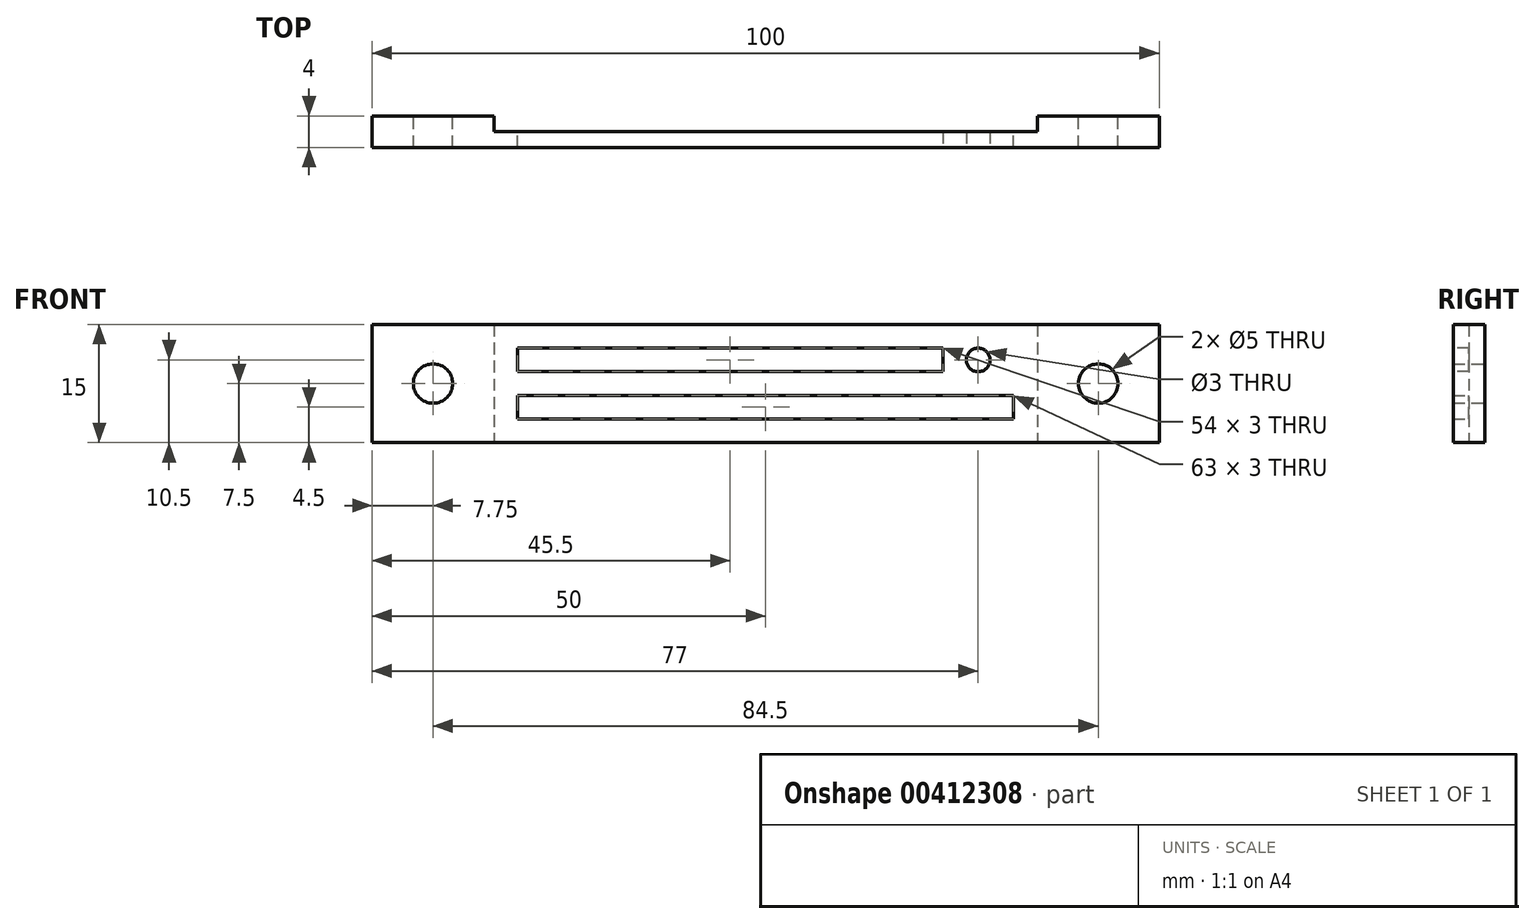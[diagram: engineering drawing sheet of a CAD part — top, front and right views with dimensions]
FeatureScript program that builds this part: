
annotation { "Feature Type Name" : "Feature", "Feature Type Description" : "" }
export const myFeature = defineFeature(function(context is Context, id is Id, definition is map)
    precondition{}
    {
        {
            var Q0;
            Q0=qCreatedBy(makeId("Front.planeOp"),FACE);
            var sketch = newSketch(context, id + "F0", { "sketchPlane" : qUnion([Q0])});
            skLineSegment(sketch, "E0.bottom", {"start": v(50, 7.5) * mm, "end": v(-50, 7.5) * mm});
            skLineSegment(sketch, "E0.top", {"start": v(50, -7.5) * mm, "end": v(-50, -7.5) * mm});
            skLineSegment(sketch, "E0.left", {"start": v(50, 7.5) * mm, "end": v(50, -7.5) * mm});
            skLineSegment(sketch, "E0.right", {"start": v(-50, 7.5) * mm, "end": v(-50, -7.5) * mm});
            skPoint(sketch, "E0.middle", {"position": v(0, 0) * mm});
            skLineSegment(sketch, "E1.bottom", {"start": v(31.5, 4.5) * mm, "end": v(-31.5, 4.5) * mm});
            skLineSegment(sketch, "E1.top", {"start": v(31.5, 1.5) * mm, "end": v(-31.5, 1.5) * mm});
            skLineSegment(sketch, "E1.left", {"start": v(31.5, 4.5) * mm, "end": v(31.5, 1.5) * mm});
            skLineSegment(sketch, "E1.right", {"start": v(-31.5, 4.5) * mm, "end": v(-31.5, 1.5) * mm});
            skPoint(sketch, "E1.middle", {"position": v(0, 3) * mm});
            skLineSegment(sketch, "E2.bottom", {"start": v(31.5, -1.5) * mm, "end": v(-31.5, -1.5) * mm});
            skLineSegment(sketch, "E2.top", {"start": v(31.5, -4.5) * mm, "end": v(-31.5, -4.5) * mm});
            skLineSegment(sketch, "E2.left", {"start": v(31.5, -1.5) * mm, "end": v(31.5, -4.5) * mm});
            skLineSegment(sketch, "E2.right", {"start": v(-31.5, -1.5) * mm, "end": v(-31.5, -4.5) * mm});
            skPoint(sketch, "E2.middle", {"position": v(0, -3) * mm});
            skSolve(sketch);
        }
        {
            var Q0;
            Q0 = qSketchRegion(id + "F0", true);
            extrude(context, id + "F1", {"entities" : qUnion([Q0]), "depth" : 4 * mm});
        }
        {
            var Q0;
            Q0=makeQuery(id+"F1.opExtrude","CAP_FACE",FACE,{"disambiguationData":[OSD([sQuery(id+"F0.wireOp",EDGE,"E0.bottom"),sQuery(id+"F0.wireOp",EDGE,"E0.top"),sQuery(id+"F0.wireOp",EDGE,"E0.left"),sQuery(id+"F0.wireOp",EDGE,"E0.right"),sQuery(id+"F0.wireOp",EDGE,"E1.bottom"),sQuery(id+"F0.wireOp",EDGE,"E1.top"),sQuery(id+"F0.wireOp",EDGE,"E1.left"),sQuery(id+"F0.wireOp",EDGE,"E1.right"),sQuery(id+"F0.wireOp",EDGE,"E2.bottom"),sQuery(id+"F0.wireOp",EDGE,"E2.top"),sQuery(id+"F0.wireOp",EDGE,"E2.left"),sQuery(id+"F0.wireOp",EDGE,"E2.right")])],"isStart":true});
            var sketch = newSketch(context, id + "F2", { "sketchPlane" : qUnion([Q0])});
            skLineSegment(sketch, "E3.bottom", {"start": v(34.5, 7.5) * mm, "end": v(-34.5, 7.5) * mm});
            skLineSegment(sketch, "E3.top", {"start": v(34.5, -7.5) * mm, "end": v(-34.5, -7.5) * mm});
            skLineSegment(sketch, "E3.left", {"start": v(34.5, 7.5) * mm, "end": v(34.5, -7.5) * mm});
            skLineSegment(sketch, "E3.right", {"start": v(-34.5, 7.5) * mm, "end": v(-34.5, -7.5) * mm});
            skPoint(sketch, "E3.middle", {"position": v(0, 0) * mm});
            skSolve(sketch);
        }
        {
            var Q0;
            Q0 = qSketchRegion(id + "F2", true);
            extrude(context, id + "F3", {"entities" : qUnion([Q0]), "operationType" : NewBodyOperationType.REMOVE, "oppositeDirection" : true, "depth" : 2 * mm});
        }
        {
            var Q0;
            {var subQ0=sQuery(id+"F0.wireOp",EDGE,"E0.bottom");var subQ1=sQuery(id+"F0.wireOp",EDGE,"E0.top");var subQ2=sQuery(id+"F0.wireOp",EDGE,"E0.left");Q0=makeQuery(id+"F3.boolean.opBoolean","SPLIT",FACE,{"disambiguationData":[TD([makeQuery(id+"F1.opExtrude","SWEPT_FACE",FACE,{"disambiguationData":[OSD([subQ2])]})])],"derivedFrom":makeQuery(id+"F1.opExtrude","CAP_FACE",FACE,{"disambiguationData":[OSD([subQ0,subQ1,subQ2,sQuery(id+"F0.wireOp",EDGE,"E0.right"),sQuery(id+"F0.wireOp",EDGE,"E1.bottom"),sQuery(id+"F0.wireOp",EDGE,"E1.top"),sQuery(id+"F0.wireOp",EDGE,"E1.left"),sQuery(id+"F0.wireOp",EDGE,"E1.right"),sQuery(id+"F0.wireOp",EDGE,"E2.bottom"),sQuery(id+"F0.wireOp",EDGE,"E2.top"),sQuery(id+"F0.wireOp",EDGE,"E2.left"),sQuery(id+"F0.wireOp",EDGE,"E2.right")])],"isStart":true})});}
            var sketch = newSketch(context, id + "F4", { "sketchPlane" : qUnion([Q0])});
            skLineSegment(sketch, "E4", {"start": v(-34.5, 7.5) * mm, "end": v(-50, -7.5) * mm, "construction": true});
            skLineSegment(sketch, "E5", {"start": v(-50, -7.5) * mm, "end": v(-50, 7.5) * mm, "construction": true});
            skLineSegment(sketch, "E6", {"start": v(-50, 7.5) * mm, "end": v(-34.5, -7.5) * mm, "construction": true});
            skCircle(sketch, "E7", {"center": v(-42.25, 0) * mm, "radius": 2.5 * mm});
            skSolve(sketch);
        }
        {
            var Q0;
            Q0 = qSketchRegion(id + "F4", true);
            extrude(context, id + "F5", {"entities" : qUnion([Q0]), "operationType" : NewBodyOperationType.REMOVE, "oppositeDirection" : true, "depth" : 25 * mm});
        }
        {
            var Q0;
            {var subQ0=sQuery(id+"F0.wireOp",EDGE,"E0.bottom");var subQ1=sQuery(id+"F0.wireOp",EDGE,"E0.right");var subQ2=sQuery(id+"F0.wireOp",EDGE,"E0.top");Q0=makeQuery(id+"F3.boolean.opBoolean","SPLIT",FACE,{"disambiguationData":[TD([makeQuery(id+"F1.opExtrude","SWEPT_FACE",FACE,{"disambiguationData":[OSD([subQ1])]})])],"derivedFrom":makeQuery(id+"F1.opExtrude","CAP_FACE",FACE,{"disambiguationData":[OSD([subQ0,subQ2,sQuery(id+"F0.wireOp",EDGE,"E0.left"),subQ1,sQuery(id+"F0.wireOp",EDGE,"E1.bottom"),sQuery(id+"F0.wireOp",EDGE,"E1.top"),sQuery(id+"F0.wireOp",EDGE,"E1.left"),sQuery(id+"F0.wireOp",EDGE,"E1.right"),sQuery(id+"F0.wireOp",EDGE,"E2.bottom"),sQuery(id+"F0.wireOp",EDGE,"E2.top"),sQuery(id+"F0.wireOp",EDGE,"E2.left"),sQuery(id+"F0.wireOp",EDGE,"E2.right")])],"isStart":true})});}
            var sketch = newSketch(context, id + "F6", { "sketchPlane" : qUnion([Q0])});
            skLineSegment(sketch, "E8", {"start": v(34.5, 7.5) * mm, "end": v(50, -7.5) * mm, "construction": true});
            skCircle(sketch, "E9", {"center": v(42.25, 0) * mm, "radius": 2.5 * mm});
            skSolve(sketch);
        }
        {
            var Q0;
            Q0 = qSketchRegion(id + "F6", true);
            extrude(context, id + "F7", {"entities" : qUnion([Q0]), "operationType" : NewBodyOperationType.REMOVE, "oppositeDirection" : true, "depth" : 25 * mm});
        }
        {
            var Q0;
            Q0=makeQuery(id+"F1.opExtrude","CAP_FACE",FACE,{"disambiguationData":[OSD([sQuery(id+"F0.wireOp",EDGE,"E0.bottom"),sQuery(id+"F0.wireOp",EDGE,"E0.top"),sQuery(id+"F0.wireOp",EDGE,"E0.left"),sQuery(id+"F0.wireOp",EDGE,"E0.right"),sQuery(id+"F0.wireOp",EDGE,"E1.bottom"),sQuery(id+"F0.wireOp",EDGE,"E1.top"),sQuery(id+"F0.wireOp",EDGE,"E1.left"),sQuery(id+"F0.wireOp",EDGE,"E1.right"),sQuery(id+"F0.wireOp",EDGE,"E2.bottom"),sQuery(id+"F0.wireOp",EDGE,"E2.top"),sQuery(id+"F0.wireOp",EDGE,"E2.left"),sQuery(id+"F0.wireOp",EDGE,"E2.right")])],"isStart":false});
            var sketch = newSketch(context, id + "F8", { "sketchPlane" : qUnion([Q0])});
            skLineSegment(sketch, "E10.bottom", {"start": v(31.5, 4.5) * mm, "end": v(22.5, 4.5) * mm});
            skLineSegment(sketch, "E10.top", {"start": v(31.5, 1.5) * mm, "end": v(22.5, 1.5) * mm});
            skLineSegment(sketch, "E10.left", {"start": v(31.5, 4.5) * mm, "end": v(31.5, 1.5) * mm});
            skLineSegment(sketch, "E10.right", {"start": v(22.5, 4.5) * mm, "end": v(22.5, 1.5) * mm});
            skSolve(sketch);
        }
        {
            var Q0;
            Q0 = qSketchRegion(id + "F8", true);
            extrude(context, id + "F9", {"entities" : qUnion([Q0]), "operationType" : NewBodyOperationType.ADD, "oppositeDirection" : true, "depth" : 2 * mm});
        }
        {
            var Q0;
            Q0=makeQuery(id+"F9.boolean.opBoolean","MERGE",FACE,{"derivedFrom":[makeQuery(id+"F1.opExtrude","CAP_FACE",FACE,{"disambiguationData":[OSD([sQuery(id+"F0.wireOp",EDGE,"E0.bottom"),sQuery(id+"F0.wireOp",EDGE,"E0.top"),sQuery(id+"F0.wireOp",EDGE,"E0.left"),sQuery(id+"F0.wireOp",EDGE,"E0.right"),sQuery(id+"F0.wireOp",EDGE,"E1.bottom"),sQuery(id+"F0.wireOp",EDGE,"E1.top"),sQuery(id+"F0.wireOp",EDGE,"E1.left"),sQuery(id+"F0.wireOp",EDGE,"E1.right"),sQuery(id+"F0.wireOp",EDGE,"E2.bottom"),sQuery(id+"F0.wireOp",EDGE,"E2.top"),sQuery(id+"F0.wireOp",EDGE,"E2.left"),sQuery(id+"F0.wireOp",EDGE,"E2.right")])],"isStart":false}),makeQuery(id+"F9.opExtrude","CAP_FACE",FACE,{"disambiguationData":[OSD([sQuery(id+"F8.wireOp",EDGE,"E10.bottom"),sQuery(id+"F8.wireOp",EDGE,"E10.top"),sQuery(id+"F8.wireOp",EDGE,"E10.left"),sQuery(id+"F8.wireOp",EDGE,"E10.right")])],"isStart":true})]});
            var sketch = newSketch(context, id + "F10", { "sketchPlane" : qUnion([Q0])});
            skCircle(sketch, "E11", {"center": v(27, 3) * mm, "radius": 1.5 * mm});
            skSolve(sketch);
        }
        {
            var Q0;
            Q0 = qSketchRegion(id + "F10", true);
            extrude(context, id + "F11", {"entities" : qUnion([Q0]), "operationType" : NewBodyOperationType.REMOVE, "oppositeDirection" : true, "depth" : 25 * mm});
        }
    });
